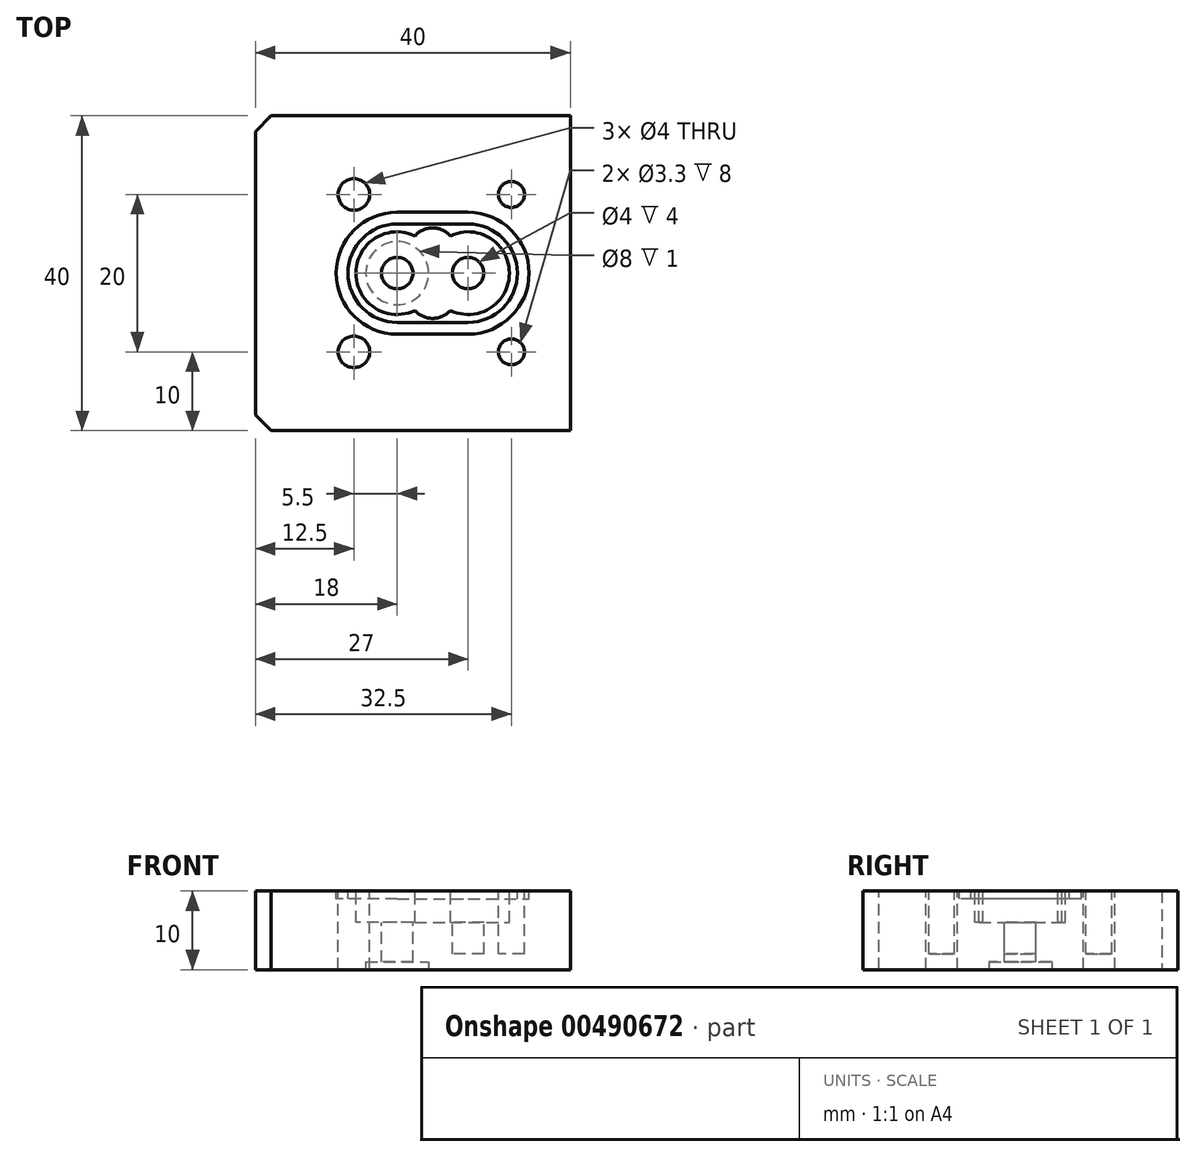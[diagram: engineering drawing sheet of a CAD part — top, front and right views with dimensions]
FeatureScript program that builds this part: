
annotation { "Feature Type Name" : "Feature", "Feature Type Description" : "" }
export const myFeature = defineFeature(function(context is Context, id is Id, definition is map)
    precondition{}
    {
        {
            var Q0;
            Q0=qCreatedBy(makeId("Top.planeOp"),FACE);
            var sketch = newSketch(context, id + "F0", { "sketchPlane" : qUnion([Q0])});
            skLineSegment(sketch, "E0.bottom", {"start": v(0, 0) * mm, "end": v(41, 0) * mm});
            skLineSegment(sketch, "E0.top", {"start": v(0, -40) * mm, "end": v(41, -40) * mm});
            skLineSegment(sketch, "E0.left", {"start": v(0, 0) * mm, "end": v(0, -40) * mm});
            skLineSegment(sketch, "E0.right", {"start": v(41, 0) * mm, "end": v(41, -40) * mm});
            skLineSegment(sketch, "E1", {"start": v(0, -20) * mm, "end": v(41, -20) * mm, "construction": true});
            skArc(sketch, "E2", {"start": v(22.74, -24.74) * mm, "mid": v(30.25, -20) * mm, "end": v(22.74, -15.26) * mm});
            skCircle(sketch, "E3", {"center": v(16, -20) * mm, "radius": 2 * mm});
            skCircle(sketch, "E4", {"center": v(25, -20) * mm, "radius": 2 * mm});
            skPoint(sketch, "E5", {"position": v(20.5, -20) * mm});
            skArc(sketch, "E6", {"start": v(16, -13.75) * mm, "mid": v(9.75, -20) * mm, "end": v(16, -26.25) * mm});
            skArc(sketch, "E7", {"start": v(25, -26.25) * mm, "mid": v(31.25, -20) * mm, "end": v(25, -13.75) * mm});
            skLineSegment(sketch, "E8", {"start": v(16, -13.75) * mm, "end": v(25, -13.75) * mm});
            skLineSegment(sketch, "E9", {"start": v(16, -26.25) * mm, "end": v(25, -26.25) * mm});
            skLineSegment(sketch, "E10.0", {"start": v(16, -27.75) * mm, "end": v(25, -27.75) * mm});
            skArc(sketch, "E10.1", {"start": v(16, -12.25) * mm, "mid": v(8.25, -20) * mm, "end": v(16, -27.75) * mm});
            skLineSegment(sketch, "E10.2", {"start": v(16, -12.25) * mm, "end": v(25, -12.25) * mm});
            skArc(sketch, "E10.3", {"start": v(25, -27.75) * mm, "mid": v(32.75, -20) * mm, "end": v(25, -12.25) * mm});
            skLineSegment(sketch, "E11", {"start": v(0, -17.25) * mm, "end": v(41, -17.25) * mm, "construction": true});
            skLineSegment(sketch, "E12", {"start": v(0, -22.75) * mm, "end": v(41, -22.75) * mm, "construction": true});
            skArc(sketch, "E13", {"start": v(22.74, -15.26) * mm, "mid": v(20.5, -14.25) * mm, "end": v(18.26, -15.26) * mm});
            skArc(sketch, "E14", {"start": v(18.26, -24.74) * mm, "mid": v(20.5, -25.75) * mm, "end": v(22.74, -24.74) * mm});
            skArc(sketch, "E15.trimOffspring", {"start": v(18.26, -15.26) * mm, "mid": v(10.75, -20) * mm, "end": v(18.26, -24.74) * mm});
            skArc(sketch, "E16.0", {"start": v(16, -12.95) * mm, "mid": v(8.95, -20) * mm, "end": v(16, -27.05) * mm, "construction": true});
            skLineSegment(sketch, "E16.1", {"start": v(16, -12.95) * mm, "end": v(25, -12.95) * mm, "construction": true});
            skArc(sketch, "E16.2", {"start": v(25, -27.05) * mm, "mid": v(32.05, -20) * mm, "end": v(25, -12.95) * mm, "construction": true});
            skLineSegment(sketch, "E16.3", {"start": v(16, -27.05) * mm, "end": v(25, -27.05) * mm, "construction": true});
            skLineSegment(sketch, "E17", {"start": v(20.5, -40) * mm, "end": v(20.5, 0) * mm, "construction": true});
            skLineSegment(sketch, "E18", {"start": v(0, -30) * mm, "end": v(41, -30) * mm, "construction": true});
            skLineSegment(sketch, "E19", {"start": v(0, -10) * mm, "end": v(41, -10) * mm, "construction": true});
            skLineSegment(sketch, "E20", {"start": v(10.5, -40) * mm, "end": v(10.5, 0) * mm, "construction": true});
            skLineSegment(sketch, "E21", {"start": v(30.5, -40) * mm, "end": v(30.5, 0) * mm, "construction": true});
            skCircle(sketch, "E22", {"center": v(10.5, -30) * mm, "radius": 2 * mm});
            skCircle(sketch, "E23", {"center": v(10.5, -10) * mm, "radius": 2 * mm});
            skCircle(sketch, "E24", {"center": v(30.5, -30) * mm, "radius": 1.65 * mm});
            skCircle(sketch, "E25", {"center": v(30.5, -10) * mm, "radius": 1.65 * mm});
            skSolve(sketch);
        }
        {
            var Q0;
            Q0=makeQuery(id+"F0.imprint","IMPRINT",FACE,{"disambiguationData":[TD([[makeQuery(id+"F0.imprint","IMPRINT",EDGE,{"derivedFrom":sQuery(id+"F0.wireOp",EDGE,"E0.bottom")}),-1.0]])]});
            var Q1;
            Q1=makeQuery(id+"F0.imprint","IMPRINT",FACE,{"disambiguationData":[TD([[makeQuery(id+"F0.imprint","IMPRINT",EDGE,{"derivedFrom":sQuery(id+"F0.wireOp",EDGE,"MZw8L1mY-04MB-L0nq-oH4W-q9KqwQQnYDyC")}),-1.0]])]});
            var Q2;
            Q2=makeQuery(id+"F0.imprint","IMPRINT",FACE,{"disambiguationData":[TD([[makeQuery(id+"F0.imprint","IMPRINT",EDGE,{"derivedFrom":sQuery(id+"F0.wireOp",EDGE,"MZw8L1mY-04MB-L0nq-oH4W-q9KqwQQnYDyC")}),1.0]])]});
            var Q3;
            Q3=makeQuery(id+"F0.imprint","IMPRINT",FACE,{"disambiguationData":[TD([[makeQuery(id+"F0.imprint","IMPRINT",EDGE,{"derivedFrom":sQuery(id+"F0.wireOp",EDGE,"E4")}),1.0]])]});
            var Q4;
            Q4=makeQuery(id+"F0.imprint","IMPRINT",FACE,{"disambiguationData":[TD([[makeQuery(id+"F0.imprint","IMPRINT",EDGE,{"derivedFrom":sQuery(id+"F0.wireOp",EDGE,"E6")}),-1.0]])]});
            var Q5;
            Q5=makeQuery(id+"F0.imprint","IMPRINT",FACE,{"disambiguationData":[TD([[makeQuery(id+"F0.imprint","IMPRINT",EDGE,{"derivedFrom":sQuery(id+"F0.wireOp",EDGE,"E2")}),1.0]])]});
            var Q6;
            Q6=makeQuery(id+"F0.imprint","IMPRINT",FACE,{"disambiguationData":[TD([[makeQuery(id+"F0.imprint","IMPRINT",EDGE,{"derivedFrom":sQuery(id+"F0.wireOp",EDGE,"E2")}),-1.0]])]});
            var Q7;
            Q7=makeQuery(id+"F0.imprint","IMPRINT",FACE,{"disambiguationData":[TD([[makeQuery(id+"F0.imprint","IMPRINT",EDGE,{"derivedFrom":sQuery(id+"F0.wireOp",EDGE,"ea91da5f-1847-4e72-b56f-cc8c6eb2f272.0.1.0")}),1.0]])]});
            var Q8;
            Q8=makeQuery(id+"F0.imprint","IMPRINT",FACE,{"disambiguationData":[TD([[makeQuery(id+"F0.imprint","IMPRINT",EDGE,{"derivedFrom":sQuery(id+"F0.wireOp",EDGE,"ea91da5f-1847-4e72-b56f-cc8c6eb2f272.1.0.0")}),1.0]])]});
            var Q9;
            Q9=makeQuery(id+"F0.imprint","IMPRINT",FACE,{"disambiguationData":[TD([[makeQuery(id+"F0.imprint","IMPRINT",EDGE,{"derivedFrom":sQuery(id+"F0.wireOp",EDGE,"E25")}),1.0]])]});
            var Q10;
            Q10=makeQuery(id+"F0.imprint","IMPRINT",FACE,{"disambiguationData":[TD([[makeQuery(id+"F0.imprint","IMPRINT",EDGE,{"derivedFrom":sQuery(id+"F0.wireOp",EDGE,"E24")}),1.0]])]});
            extrude(context, id + "F1", {"entities" : qUnion([Q0, Q1, Q2, Q3, Q4, Q5, Q6, Q7, Q8, Q9, Q10]), "oppositeDirection" : true, "depth" : 10 * mm, "offsetDistance" : 25 * mm});
        }
        {
            var Q0;
            Q0=makeQuery(id+"F0.imprint","IMPRINT",FACE,{"disambiguationData":[TD([[makeQuery(id+"F0.imprint","IMPRINT",EDGE,{"derivedFrom":sQuery(id+"F0.wireOp",EDGE,"E6")}),-1.0]])]});
            extrude(context, id + "F2", {"entities" : qUnion([Q0]), "operationType" : NewBodyOperationType.REMOVE, "oppositeDirection" : true, "depth" : 1 * mm, "offsetDistance" : 25 * mm});
        }
        {
            var Q0;
            Q0=makeQuery(id+"F0.imprint","IMPRINT",FACE,{"disambiguationData":[TD([[makeQuery(id+"F0.imprint","IMPRINT",EDGE,{"derivedFrom":sQuery(id+"F0.wireOp",EDGE,"E4")}),1.0]])]});
            extrude(context, id + "F3", {"entities" : qUnion([Q0]), "operationType" : NewBodyOperationType.REMOVE, "oppositeDirection" : true, "depth" : 8 * mm, "offsetDistance" : 25 * mm});
        }
        {
            var Q0;
            Q0=makeQuery(id+"F0.imprint","IMPRINT",FACE,{"disambiguationData":[TD([[makeQuery(id+"F0.imprint","IMPRINT",EDGE,{"derivedFrom":sQuery(id+"F0.wireOp",EDGE,"E2")}),1.0]])]});
            extrude(context, id + "F4", {"entities" : qUnion([Q0]), "operationType" : NewBodyOperationType.REMOVE, "oppositeDirection" : true, "depth" : 4 * mm, "offsetDistance" : 25 * mm});
        }
        {
            var Q0;
            Q0=makeQuery(id+"F1.opExtrude","CAP_FACE",FACE,{"disambiguationData":[OSD([sQuery(id+"F0.wireOp",EDGE,"E0.bottom"),sQuery(id+"F0.wireOp",EDGE,"E0.top"),sQuery(id+"F0.wireOp",EDGE,"E0.left"),sQuery(id+"F0.wireOp",EDGE,"E0.right"),sQuery(id+"F0.wireOp",EDGE,"E3"),sQuery(id+"F0.wireOp",EDGE,"0gURjQAW-o9TF-LYW3-5VQh-sVZyAbxpT9Lx"),sQuery(id+"F0.wireOp",EDGE,"ea91da5f-1847-4e72-b56f-cc8c6eb2f272.0.1.0"),sQuery(id+"F0.wireOp",EDGE,"ea91da5f-1847-4e72-b56f-cc8c6eb2f272.1.0.0"),sQuery(id+"F0.wireOp",EDGE,"ea91da5f-1847-4e72-b56f-cc8c6eb2f272.1.1.0")])],"isStart":false});
            var sketch = newSketch(context, id + "F5", { "sketchPlane" : qUnion([Q0])});
            skLineSegment(sketch, "E26", {"start": v(20.5, 0) * mm, "end": v(20.5, 40) * mm, "construction": true});
            skCircle(sketch, "E27", {"center": v(20.5, 3) * mm, "radius": 1.25 * mm});
            skCircle(sketch, "E28", {"center": v(20.5, 37) * mm, "radius": 1.25 * mm});
            skCircle(sketch, "E29", {"center": v(16, 20) * mm, "radius": 4 * mm});
            skSolve(sketch);
        }
        {
            var Q0;
            Q0=makeQuery(id+"F5.imprint","IMPRINT",FACE,{"disambiguationData":[TD([[makeQuery(id+"F5.imprint","IMPRINT",EDGE,{"derivedFrom":sQuery(id+"F5.wireOp",EDGE,"E29")}),1.0]])]});
            extrude(context, id + "F6", {"entities" : qUnion([Q0]), "operationType" : NewBodyOperationType.REMOVE, "oppositeDirection" : true, "depth" : 1 * mm, "offsetDistance" : 25 * mm});
        }
        {
            var Q0;
            Q0=makeQuery(id+"F0.imprint","IMPRINT",FACE,{"disambiguationData":[TD([[makeQuery(id+"F0.imprint","IMPRINT",EDGE,{"derivedFrom":sQuery(id+"F0.wireOp",EDGE,"E24")}),1.0]])]});
            var Q1;
            Q1=makeQuery(id+"F0.imprint","IMPRINT",FACE,{"disambiguationData":[TD([[makeQuery(id+"F0.imprint","IMPRINT",EDGE,{"derivedFrom":sQuery(id+"F0.wireOp",EDGE,"E25")}),1.0]])]});
            extrude(context, id + "F7", {"entities" : qUnion([Q0, Q1]), "operationType" : NewBodyOperationType.REMOVE, "oppositeDirection" : true, "depth" : 8 * mm, "offsetDistance" : 25 * mm});
        }
        {
            var Q0;
            Q0=makeQuery(id+"F1.opExtrude","SWEPT_FACE",FACE,{"disambiguationData":[OSD([sQuery(id+"F0.wireOp",EDGE,"E0.left")])]});
            extrude(context, id + "F8", {"entities" : qUnion([Q0]), "operationType" : NewBodyOperationType.ADD, "depth" : 2 * mm, "offsetDistance" : 25 * mm});
        }
        {
            var Q0;
            Q0=makeQuery(id+"F8.opExtrude","CAP_EDGE",EDGE,{"disambiguationData":[OSD([sQuery(id+"F0.wireOp",EDGE,"E0.top"),sQuery(id+"F0.wireOp",EDGE,"E0.left")])],"isStart":false});
            var Q1;
            Q1=makeQuery(id+"F8.opExtrude","CAP_EDGE",EDGE,{"disambiguationData":[OSD([sQuery(id+"F0.wireOp",EDGE,"E0.bottom"),sQuery(id+"F0.wireOp",EDGE,"E0.left")])],"isStart":false});
            chamfer(context, id + "F9", {"entities" : qUnion([Q0, Q1]), "width" : 2 * mm, "tangentPropagation" : true});
        }
        {
            var Q0;
            Q0=makeQuery(id+"F1.opExtrude","SWEPT_FACE",FACE,{"disambiguationData":[OSD([sQuery(id+"F0.wireOp",EDGE,"E0.right")])]});
            extrude(context, id + "F10", {"entities" : qUnion([Q0]), "operationType" : NewBodyOperationType.REMOVE, "oppositeDirection" : true, "depth" : 3 * mm, "offsetDistance" : 25 * mm});
        }
    });
